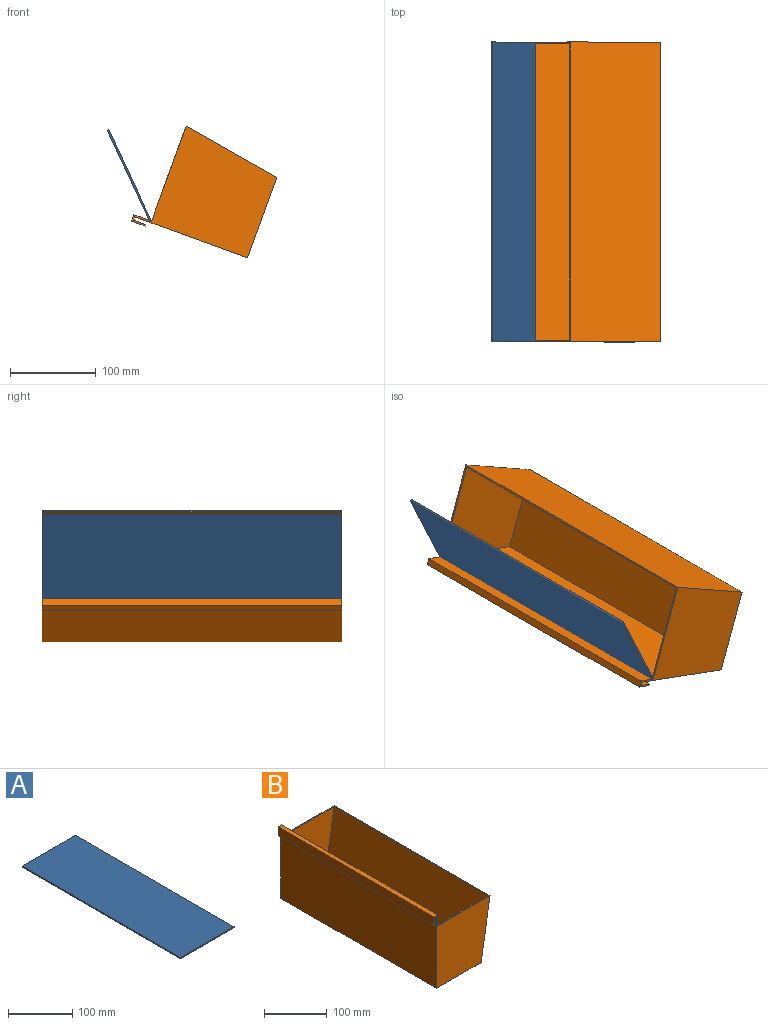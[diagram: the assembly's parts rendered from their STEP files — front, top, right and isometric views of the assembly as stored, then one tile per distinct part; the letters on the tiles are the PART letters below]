
ASSEMBLY  parts=2 mates=1
PART A: 6 faces, bbox 117.7x350x2.3 mm
  f0: plane 350x117.74mm, normal (0,0,1), area 41210.5mm2, adj f1,f3,f4,f5
  f1: plane 350x2.3mm, normal (-1,0,0), area 805mm2, adj f0,f2,f4,f5
  f2: plane 350x117.74mm, normal (0,0,-1), area 41210.5mm2, adj f1,f3,f4,f5
  f3: plane 350x2.3mm, normal (1,0,0), area 805mm2, adj f0,f2,f4,f5
  f4: plane 117.74x2.3mm, normal (0,-1,0), area 270.8mm2, adj f0,f1,f2,f3
  f5: plane 117.74x2.3mm, normal (0,1,0), area 270.8mm2, adj f0,f1,f2,f3
PART B: 16 faces, bbox 126x350x142 mm
  f0: plane 350x118mm, normal (0,0,1), area 1173.5mm2, adj f3,f4,f10,f11,f13,f14,f15
  f1: plane 350x139.98mm, normal (-1,0,0), area 48992.3mm2, adj f2,f9,f10,f11
  f2: plane 350x100mm, normal (0,0,-1), area 35000mm2, adj f1,f3,f10,f11
  f3: plane 350x120mm, normal (0.99,0,-0.16), area 42579.3mm2, adj f0,f2,f10,f11
  f4: plane 350x139.98mm, normal (1,0,0), area 48520.3mm2, adj f0,f5,f10,f11,f12,f14,f15
  f5: plane 350x8mm, normal (0,0,1), area 2800mm2, adj f4,f6,f10,f11
  f6: plane 350x17mm, normal (-1,0,0), area 5950mm2, adj f5,f7,f10,f11
  f7: plane 350x2mm, normal (0,0,-1), area 700mm2, adj f6,f8,f10,f11
  f8: plane 350x15mm, normal (1,0,0), area 5250mm2, adj f7,f9,f10,f11
  f9: plane 350x4mm, normal (0,0,-1), area 1400mm2, adj f1,f8,f10,f11
  f10: plane 141.98x126mm, normal (0,-1,0), area 13286mm2, adj f0,f1,f2,f3,f4,f5,f6,f7
  f11: plane 141.98x126mm, normal (0,1,0), area 13286mm2, adj f0,f1,f2,f3,f4,f5,f6,f7
  f12: plane 346x96.31mm, normal (0,0,1), area 33321.8mm2, adj f4,f13,f14,f15
  f13: plane 346x118mm, normal (-0.99,0,0.16), area 41391.2mm2, adj f0,f12,f14,f15
  f14: plane 118x115.97mm, normal (0,1,0), area 12524.4mm2, adj f0,f4,f12,f13
  f15: plane 118x115.97mm, normal (0,-1,0), area 12524.4mm2, adj f0,f4,f12,f13
PLACE A rot(axis=(0,-1,0),115deg) t=(-26.57,-24.06,68.47)mm
PLACE B rot(axis=(0,-1,0),70deg) t=(19.03,-24.06,24.2)mm
MATE revolute A.f4 <-> B.f10  axis (0,-1,0) through (-57.19,-199.06,-9.78)mm
